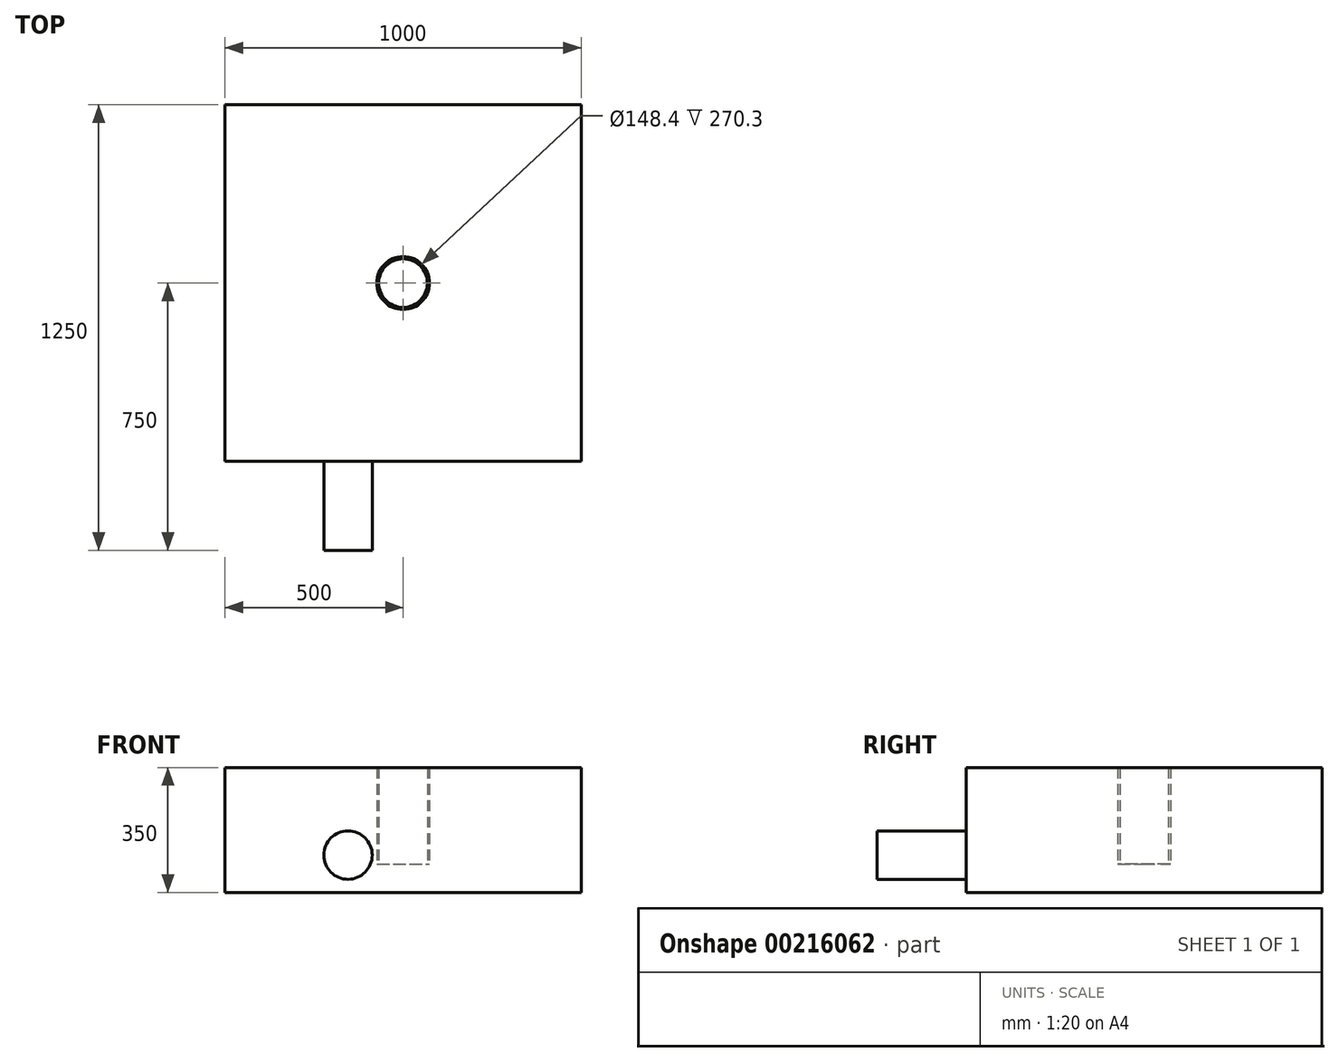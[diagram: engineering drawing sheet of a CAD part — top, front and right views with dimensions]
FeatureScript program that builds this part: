
annotation { "Feature Type Name" : "Feature", "Feature Type Description" : "" }
export const myFeature = defineFeature(function(context is Context, id is Id, definition is map)
    precondition{}
    {
        {
            var Q0;
            Q0=qCreatedBy(makeId("Front.planeOp"),FACE);
            var sketch = newSketch(context, id + "F0", { "sketchPlane" : qUnion([Q0])});
            skLineSegment(sketch, "E0", {"start": v(-74.2, 745) * mm, "end": v(-74.2, 245) * mm});
            skLineSegment(sketch, "E1", {"start": v(-74.2, 245) * mm, "end": v(-68.2, 245) * mm});
            skLineSegment(sketch, "E2", {"start": v(-68.2, 245) * mm, "end": v(-68.2, 745) * mm});
            skLineSegment(sketch, "E3", {"start": v(-68.2, 745) * mm, "end": v(-74.2, 745) * mm});
            skLineSegment(sketch, "E4", {"start": v(0, 0) * mm, "end": v(0, 556.99) * mm, "construction": true});
            skSolve(sketch);
        }
        {
            var Q0;
            Q0=qCreatedBy(makeId("Top.planeOp"),FACE);
            cPlane(context, id + "F1", {"entities" : qUnion([Q0]), "cplaneType" : CPlaneType.OFFSET, "offset" : 165.3 * mm, "width" : 150 * mm, "height" : 150 * mm});
        }
        {
            var Q0;
            Q0=qCreatedBy(id+"F1.planeOp",FACE);
            var sketch = newSketch(context, id + "F2", { "sketchPlane" : qUnion([Q0])});
            skLineSegment(sketch, "E5.bottom", {"start": v(-500, 500) * mm, "end": v(500, 500) * mm});
            skLineSegment(sketch, "E5.top", {"start": v(-500, -500) * mm, "end": v(500, -500) * mm});
            skLineSegment(sketch, "E5.left", {"start": v(-500, 500) * mm, "end": v(-500, -500) * mm});
            skLineSegment(sketch, "E5.right", {"start": v(500, 500) * mm, "end": v(500, -500) * mm});
            skPoint(sketch, "E5.middle", {"position": v(0, 0) * mm});
            skSolve(sketch);
        }
        {
            var Q0;
            Q0 = qSketchRegion(id + "F2", true);
            extrude(context, id + "F3", {"entities" : qUnion([Q0]), "depth" : 350 * mm});
        }
        {
            var Q0;
            Q0=makeQuery(id+"F0.imprint","IMPRINT",FACE,{"disambiguationData":[TD([[makeQuery(id+"F0.imprint","IMPRINT",EDGE,{"derivedFrom":sQuery(id+"F0.wireOp",EDGE,"E0")}),1.0]])]});
            var Q1;
            Q1=sQuery(id+"F0.wireOp",EDGE,"E4");
            revolve(context, id + "F4", {"operationType" : NewBodyOperationType.REMOVE, "entities" : qUnion([Q0]), "axis" : qUnion([Q1]), "revolveType" : RevolveType.FULL});
        }
        {
            var Q0;
            Q0=makeQuery(id+"F3.opExtrude","SWEPT_FACE",FACE,{"disambiguationData":[OSD([sQuery(id+"F2.wireOp",EDGE,"E5.top")])]});
            var sketch = newSketch(context, id + "F5", { "sketchPlane" : qUnion([Q0])});
            skCircle(sketch, "E6", {"center": v(-154.8, 270) * mm, "radius": 68 * mm});
            skSolve(sketch);
        }
        {
            var Q0;
            Q0=qSketchRegion(id+"F5",true);
            extrude(context, id + "F6", {"entities" : qUnion([Q0]), "operationType" : NewBodyOperationType.ADD, "depth" : 250 * mm});
        }
    });
